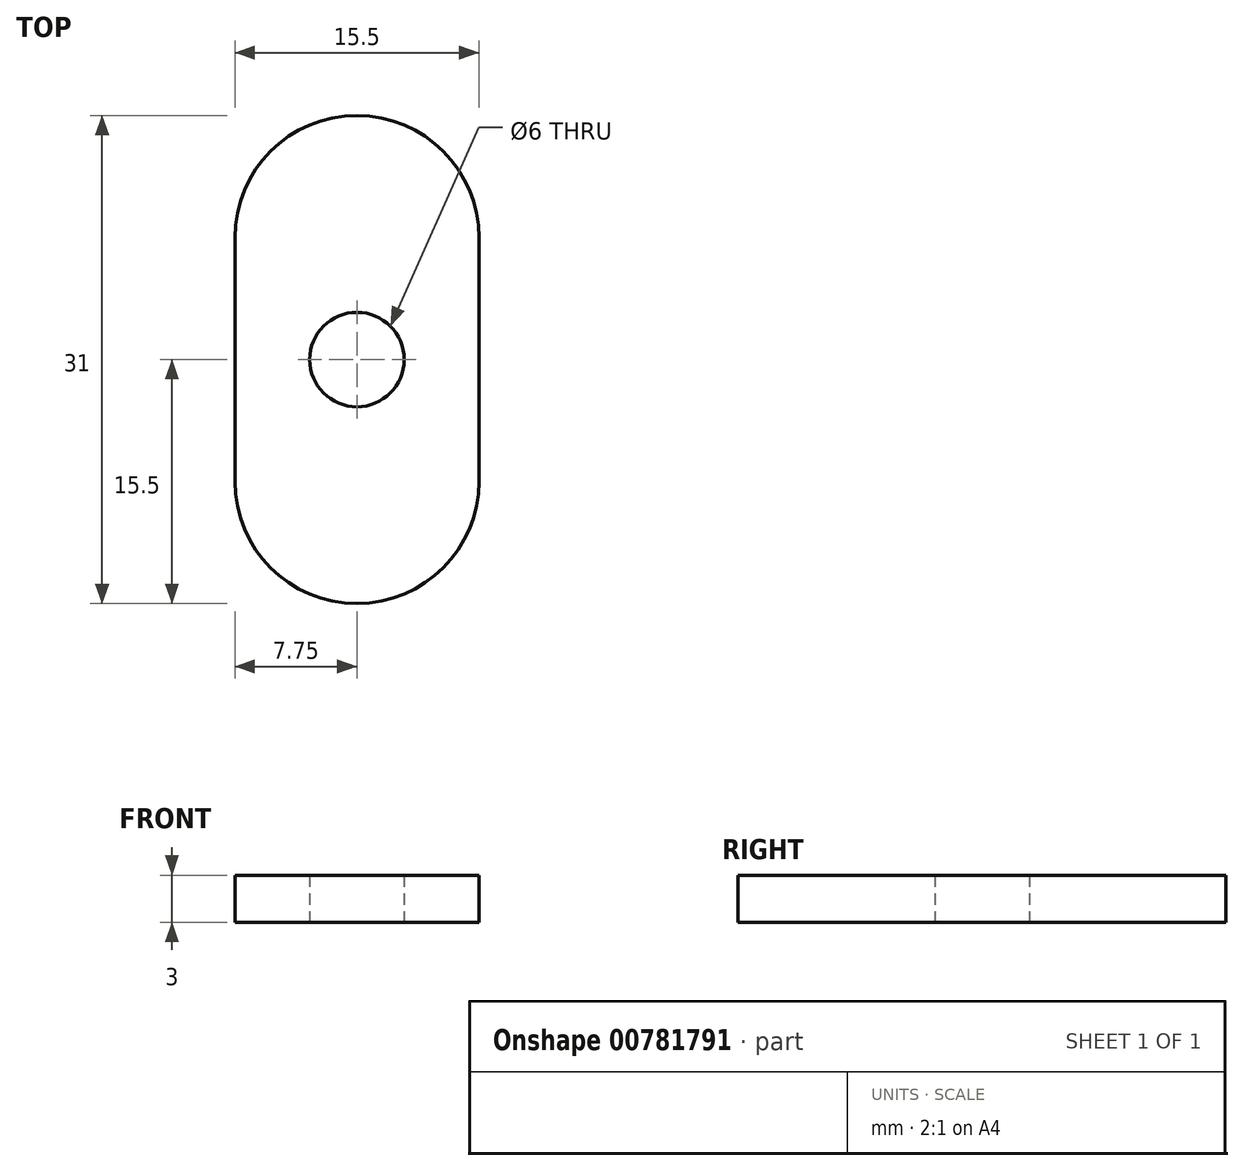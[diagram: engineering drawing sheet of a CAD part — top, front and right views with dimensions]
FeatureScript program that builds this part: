
annotation { "Feature Type Name" : "Feature", "Feature Type Description" : "" }
export const myFeature = defineFeature(function(context is Context, id is Id, definition is map)
    precondition{}
    {
        {
            var Q0;
            Q0=qCreatedBy(makeId("Top.planeOp"),FACE);
            var sketch = newSketch(context, id + "F0", { "sketchPlane" : qUnion([Q0])});
            skLineSegment(sketch, "E0.bottom", {"start": v(-7.75, 7.75) * mm, "end": v(7.75, 7.75) * mm});
            skLineSegment(sketch, "E0.top", {"start": v(-7.75, -7.75) * mm, "end": v(7.75, -7.75) * mm});
            skLineSegment(sketch, "E0.left", {"start": v(-7.75, 7.75) * mm, "end": v(-7.75, -7.75) * mm});
            skLineSegment(sketch, "E0.right", {"start": v(7.75, 7.75) * mm, "end": v(7.75, -7.75) * mm});
            skPoint(sketch, "E0.middle", {"position": v(0, 0) * mm});
            skArc(sketch, "E1", {"start": v(-7.75, 7.75) * mm, "mid": v(0, 15.5) * mm, "end": v(7.75, 7.75) * mm});
            skArc(sketch, "E2", {"start": v(-7.75, -7.75) * mm, "mid": v(0, -15.5) * mm, "end": v(7.75, -7.75) * mm});
            skCircle(sketch, "E3", {"center": v(0, 0) * mm, "radius": 3 * mm});
            skSolve(sketch);
        }
        {
            var Q0;
            Q0=makeQuery(id+"F0.imprint","IMPRINT",FACE,{"disambiguationData":[TD([[makeQuery(id+"F0.imprint","IMPRINT",EDGE,{"derivedFrom":sQuery(id+"F0.wireOp",EDGE,"E0.bottom")}),1.0]])]});
            var Q1;
            Q1=makeQuery(id+"F0.imprint","IMPRINT",FACE,{"disambiguationData":[TD([[makeQuery(id+"F0.imprint","IMPRINT",EDGE,{"derivedFrom":sQuery(id+"F0.wireOp",EDGE,"E0.bottom")}),-1.0]])]});
            var Q2;
            Q2=makeQuery(id+"F0.imprint","IMPRINT",FACE,{"disambiguationData":[TD([[makeQuery(id+"F0.imprint","IMPRINT",EDGE,{"derivedFrom":sQuery(id+"F0.wireOp",EDGE,"E0.top")}),-1.0]])]});
            extrude(context, id + "F1", {"entities" : qUnion([Q0, Q1, Q2]), "depth" : 3 * mm, "offsetDistance" : 25 * mm});
        }
    });
